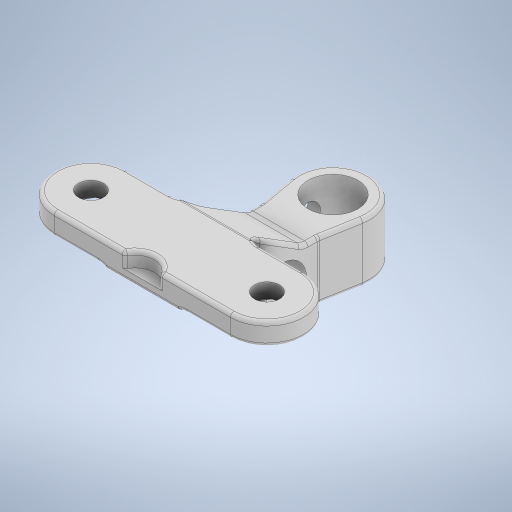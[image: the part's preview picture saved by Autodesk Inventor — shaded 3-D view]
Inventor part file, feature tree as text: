
AUTODESK INVENTOR PART (.ipt)
format: ipt  version: 2024.2 (Build 282272000, 272)  size: 527,360 bytes
history: native  units: mm
features: extrude x9, sketch x8, fillet x5, plane x3, projected_geometry x3
ambient origin geometry x8: Origin, YZ Plane, XZ Plane, XY Plane, X Axis, Y Axis, Z Axis, Center Point
bodies: Solid1 (feature_tree)
feature tree (28):
  extrude  "Extrusion1"  Depth=12.0mm
  extrude  "Extrusion2"  Depth=10.0mm
  sketch  "Sketch3"  dims[d5=3.0mm d6=0.0mm d7=5.7mm]
  extrude  "Extrusion3"  Depth=5.7mm
  extrude  "Extrusion4"  Depth=6.8mm
  plane  "Work Plane1"
  extrude  "Extrusion10"  Depth=8.0mm TaperAngle=0.0deg
  extrude  "Extrusion12"  Depth=6.0mm
  plane  "Work Plane5"
  extrude  "Extrusion13"  Depth=6.8mm
  plane  "Work Plane4"
  extrude  "Extrusion14"  Depth=10.0mm TaperAngle=0.0deg
  extrude  "Extrusion15"  Depth=2.8mm
  fillet  "Fillet14"  Radius=10.0mm
  fillet  "Fillet13"  Radius=2.0mm
  fillet  "Fillet15"  Radius=2.8mm
  fillet  "Fillet16"  Radius=10.0mm
  fillet  "Fillet17"  Radius=6.0mm
  sketch  "Sketch1"  dims[d0=24.0mm d1=12.0mm]
  sketch  "Sketch2"  dims[d2=3.4mm d4=10.0mm]
  sketch  "Sketch8"  dims[d8=1.0mm d9=0.0mm d10=6.8mm]
  sketch  "Sketch10"  dims[d11=10.0mm d13=8.0mm d14=0.0mm]
  projected_geometry  "Projected Loop3"
  sketch  "Sketch11"  dims[d15=8.0mm d16=0.0mm d17=6.0mm]
  sketch  "Sketch12"  dims[d41=10.0mm d42=6.8mm]
  sketch  "Sketch13"  dims[d44=8.0mm d45=0.0mm d49=10.0mm d50=0.0mm d51=2.8mm d52=10.0mm d53=0.0mm d54=2.0mm d55=2.8mm d56=10.0mm d57=0.0mm d61=6.0mm d62=5.25mm d63=2.0mm d64=0.0mm d66=2.0mm d67=6.0mm d68=10.0mm d69=6.0mm d74=2.0mm d75=0.5mm d76=0.5mm d77=0.5mm d78=0.5mm d28=0.0mm d29=0.0mm d30=0.0mm d31=0.0mm d32=0.0mm d39=0.0mm d40=0.0mm d73=0.0mm d79=0.0mm d80=0.0mm]
  projected_geometry  "Projected Loop4"
  projected_geometry  "Projected Loop5"
